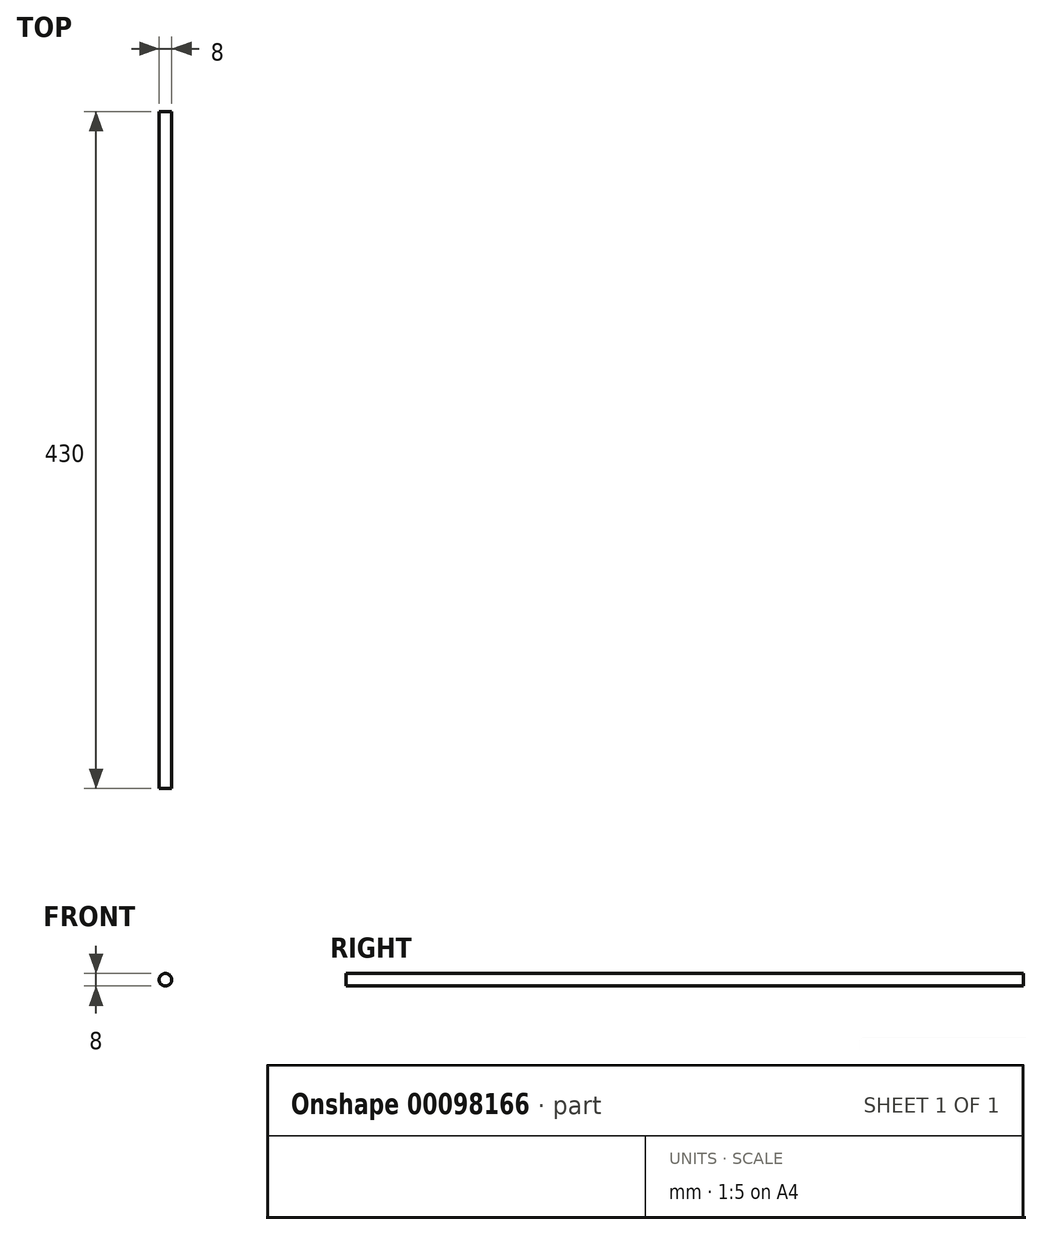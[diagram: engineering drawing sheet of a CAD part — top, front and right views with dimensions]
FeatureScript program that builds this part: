
annotation { "Feature Type Name" : "Feature", "Feature Type Description" : "" }
export const myFeature = defineFeature(function(context is Context, id is Id, definition is map)
    precondition{}
    {
        {
            var Q0;
            Q0=qCreatedBy(makeId("Front.planeOp"),FACE);
            var sketch = newSketch(context, id + "F0", { "sketchPlane" : qUnion([Q0])});
            skCircle(sketch, "E0", {"center": v(-41.14, 40.28) * mm, "radius": 4 * mm});
            skSolve(sketch);
        }
        {
            var Q0;
            Q0=makeQuery(id+"F0.imprint","IMPRINT",FACE,{"disambiguationData":[TD([[makeQuery(id+"F0.imprint","IMPRINT",EDGE,{"derivedFrom":sQuery(id+"F0.wireOp",EDGE,"E0")}),1.0]])]});
            extrude(context, id + "F1", {"entities" : qUnion([Q0]), "depth" : 430 * mm});
        }
    });
